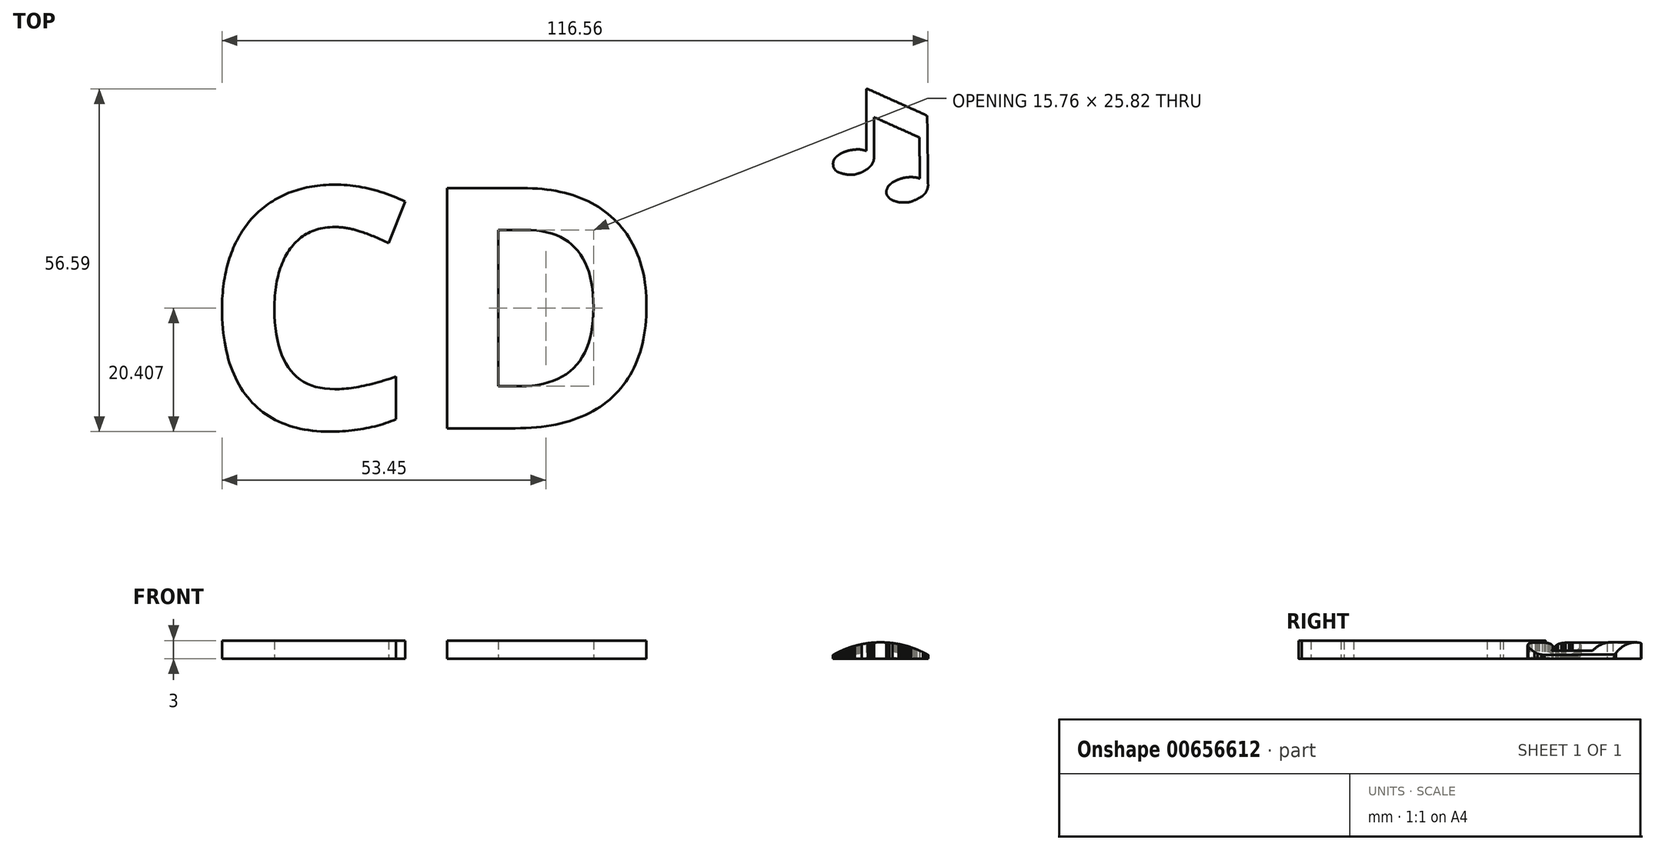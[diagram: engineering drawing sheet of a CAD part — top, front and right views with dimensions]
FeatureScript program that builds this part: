
annotation { "Feature Type Name" : "Feature", "Feature Type Description" : "" }
export const myFeature = defineFeature(function(context is Context, id is Id, definition is map)
    precondition{}
    {
        {
            var Q0;
            Q0=qCreatedBy(makeId("Top.planeOp"),FACE);
            var sketch = newSketch(context, id + "F0", { "sketchPlane" : qUnion([Q0])});
            skText(sketch, "E0", { "text": "CD", "fontName": "OpenSans-Bold.ttf"});
            const initialGuessF0  = {"E0": [-0.08042, -0.00379, 1, 0, 0.04]};
            skSetInitialGuess(sketch, initialGuessF0);
            skSolve(sketch);
        }
        {
            var Q0;
            Q0=makeQuery(id+"F0.imprint","IMPRINT",FACE,{"disambiguationData":[TD([[makeQuery(id+"F0.imprint","IMPRINT",EDGE,{"derivedFrom":sQuery(id+"F0.wireOp",EDGE,"E0.sketch_text.stroke-15")}),-1.0]])]});
            var Q1;
            Q1=makeQuery(id+"F0.imprint","IMPRINT",FACE,{"disambiguationData":[TD([[makeQuery(id+"F0.imprint","IMPRINT",EDGE,{"derivedFrom":sQuery(id+"F0.wireOp",EDGE,"E0.sketch_text.stroke-0")}),-1.0]])]});
            extrude(context, id + "F1", {"entities" : qUnion([Q0, Q1]), "depth" : 3 * mm, "offsetDistance" : 25 * mm});
        }
        {
            var Q0;
            Q0=qCreatedBy(makeId("Top.planeOp"),FACE);
            var sketch = newSketch(context, id + "F2", { "sketchPlane" : qUnion([Q0])});
            skLineSegment(sketch, "E1", {"start": v(39.37, 36.26) * mm, "end": v(39.32, 36.01) * mm});
            skLineSegment(sketch, "E2", {"start": v(39.32, 36.01) * mm, "end": v(39.27, 35.76) * mm});
            skLineSegment(sketch, "E3", {"start": v(39.27, 35.76) * mm, "end": v(38.98, 35.1) * mm});
            skLineSegment(sketch, "E4", {"start": v(38.98, 35.1) * mm, "end": v(38.39, 34.5) * mm});
            skLineSegment(sketch, "E5", {"start": v(38.39, 34.5) * mm, "end": v(38.17, 34.37) * mm});
            skLineSegment(sketch, "E6", {"start": v(38.17, 34.37) * mm, "end": v(37.95, 34.24) * mm});
            skLineSegment(sketch, "E7", {"start": v(37.95, 34.24) * mm, "end": v(37.72, 34.12) * mm});
            skLineSegment(sketch, "E8", {"start": v(37.72, 34.12) * mm, "end": v(37.5, 34.01) * mm});
            skLineSegment(sketch, "E9", {"start": v(37.5, 34.01) * mm, "end": v(37.26, 33.9) * mm});
            skLineSegment(sketch, "E10", {"start": v(37.26, 33.9) * mm, "end": v(37.03, 33.8) * mm});
            skLineSegment(sketch, "E11", {"start": v(37.03, 33.8) * mm, "end": v(36.79, 33.71) * mm});
            skLineSegment(sketch, "E12", {"start": v(36.55, 33.62) * mm, "end": v(36.42, 33.6) * mm});
            skLineSegment(sketch, "E13", {"start": v(36.42, 33.6) * mm, "end": v(36.3, 33.57) * mm});
            skLineSegment(sketch, "E14", {"start": v(36.3, 33.57) * mm, "end": v(36.17, 33.54) * mm});
            skLineSegment(sketch, "E15", {"start": v(36.17, 33.54) * mm, "end": v(36.04, 33.53) * mm});
            skLineSegment(sketch, "E16", {"start": v(36.04, 33.53) * mm, "end": v(35.91, 33.51) * mm});
            skLineSegment(sketch, "E17", {"start": v(35.91, 33.51) * mm, "end": v(35.78, 33.5) * mm});
            skLineSegment(sketch, "E18", {"start": v(35.78, 33.5) * mm, "end": v(35.65, 33.5) * mm});
            skLineSegment(sketch, "E19", {"start": v(35.65, 33.5) * mm, "end": v(35.52, 33.5) * mm});
            skLineSegment(sketch, "E20", {"start": v(35.52, 33.5) * mm, "end": v(35.26, 33.5) * mm});
            skLineSegment(sketch, "E21", {"start": v(35.26, 33.5) * mm, "end": v(35, 33.5) * mm});
            skLineSegment(sketch, "E22", {"start": v(35, 33.5) * mm, "end": v(34.74, 33.53) * mm});
            skLineSegment(sketch, "E23", {"start": v(34.74, 33.53) * mm, "end": v(34.48, 33.55) * mm});
            skLineSegment(sketch, "E24", {"start": v(34.48, 33.55) * mm, "end": v(33.53, 33.84) * mm});
            skLineSegment(sketch, "E25", {"start": v(33.53, 33.84) * mm, "end": v(33.01, 34.14) * mm});
            skLineSegment(sketch, "E26", {"start": v(33.01, 34.14) * mm, "end": v(32.57, 34.73) * mm});
            skLineSegment(sketch, "E27", {"start": v(32.57, 34.73) * mm, "end": v(32.54, 34.82) * mm});
            skLineSegment(sketch, "E28", {"start": v(32.54, 34.82) * mm, "end": v(32.52, 34.9) * mm});
            skLineSegment(sketch, "E29", {"start": v(32.52, 34.9) * mm, "end": v(32.5, 35) * mm});
            skLineSegment(sketch, "E30", {"start": v(32.5, 35) * mm, "end": v(32.49, 35.1) * mm});
            skLineSegment(sketch, "E31", {"start": v(32.49, 35.1) * mm, "end": v(32.48, 35.18) * mm});
            skLineSegment(sketch, "E32", {"start": v(32.48, 35.18) * mm, "end": v(32.48, 35.28) * mm});
            skLineSegment(sketch, "E33", {"start": v(32.48, 35.28) * mm, "end": v(32.49, 35.37) * mm});
            skLineSegment(sketch, "E34", {"start": v(32.49, 35.37) * mm, "end": v(32.5, 35.46) * mm});
            skLineSegment(sketch, "E35", {"start": v(32.5, 35.46) * mm, "end": v(32.79, 36.2) * mm});
            skLineSegment(sketch, "E36", {"start": v(32.79, 36.2) * mm, "end": v(33.45, 36.8) * mm});
            skLineSegment(sketch, "E37", {"start": v(33.45, 36.8) * mm, "end": v(33.6, 36.88) * mm});
            skLineSegment(sketch, "E38", {"start": v(33.6, 36.88) * mm, "end": v(33.76, 36.96) * mm});
            skLineSegment(sketch, "E39", {"start": v(33.76, 36.96) * mm, "end": v(33.92, 37.04) * mm});
            skLineSegment(sketch, "E40", {"start": v(33.92, 37.04) * mm, "end": v(34.08, 37.12) * mm});
            skLineSegment(sketch, "E41", {"start": v(34.08, 37.12) * mm, "end": v(34.24, 37.19) * mm});
            skLineSegment(sketch, "E42", {"start": v(34.24, 37.19) * mm, "end": v(34.4, 37.26) * mm});
            skLineSegment(sketch, "E43", {"start": v(34.4, 37.26) * mm, "end": v(34.56, 37.32) * mm});
            skLineSegment(sketch, "E44", {"start": v(34.56, 37.32) * mm, "end": v(34.73, 37.38) * mm});
            skLineSegment(sketch, "E45", {"start": v(34.73, 37.38) * mm, "end": v(34.9, 37.44) * mm});
            skLineSegment(sketch, "E46", {"start": v(34.9, 37.44) * mm, "end": v(35.07, 37.5) * mm});
            skLineSegment(sketch, "E47", {"start": v(35.07, 37.5) * mm, "end": v(35.24, 37.54) * mm});
            skLineSegment(sketch, "E48", {"start": v(35.24, 37.54) * mm, "end": v(35.4, 37.58) * mm});
            skLineSegment(sketch, "E49", {"start": v(35.4, 37.58) * mm, "end": v(35.58, 37.6) * mm});
            skLineSegment(sketch, "E50", {"start": v(35.58, 37.6) * mm, "end": v(35.75, 37.64) * mm});
            skLineSegment(sketch, "E51", {"start": v(35.75, 37.64) * mm, "end": v(35.93, 37.66) * mm});
            skLineSegment(sketch, "E52", {"start": v(35.93, 37.66) * mm, "end": v(36.1, 37.67) * mm});
            skLineSegment(sketch, "E53", {"start": v(36.1, 37.67) * mm, "end": v(36.28, 37.68) * mm});
            skLineSegment(sketch, "E54", {"start": v(36.28, 37.68) * mm, "end": v(36.45, 37.69) * mm});
            skLineSegment(sketch, "E55", {"start": v(36.45, 37.69) * mm, "end": v(36.63, 37.69) * mm});
            skLineSegment(sketch, "E56", {"start": v(36.63, 37.69) * mm, "end": v(36.8, 37.68) * mm});
            skLineSegment(sketch, "E57", {"start": v(36.8, 37.68) * mm, "end": v(36.98, 37.67) * mm});
            skLineSegment(sketch, "E58", {"start": v(36.98, 37.67) * mm, "end": v(37.16, 37.65) * mm});
            skLineSegment(sketch, "E59", {"start": v(37.16, 37.65) * mm, "end": v(37.33, 37.63) * mm});
            skLineSegment(sketch, "E60", {"start": v(37.33, 37.63) * mm, "end": v(37.5, 37.6) * mm});
            skLineSegment(sketch, "E61", {"start": v(37.5, 37.6) * mm, "end": v(38.02, 37.45) * mm});
            skLineSegment(sketch, "E62", {"start": v(38.02, 37.45) * mm, "end": v(37.94, 44.23) * mm});
            skLineSegment(sketch, "E63", {"start": v(37.94, 44.23) * mm, "end": v(32.72, 46.59) * mm});
            skLineSegment(sketch, "E64", {"start": v(32.72, 46.59) * mm, "end": v(30.46, 47.57) * mm});
            skLineSegment(sketch, "E65", {"start": v(30.46, 40.88) * mm, "end": v(30.41, 40.6) * mm});
            skLineSegment(sketch, "E66", {"start": v(30.41, 40.6) * mm, "end": v(30.36, 40.33) * mm});
            skLineSegment(sketch, "E67", {"start": v(30.36, 40.33) * mm, "end": v(30.06, 39.74) * mm});
            skLineSegment(sketch, "E68", {"start": v(30.06, 39.74) * mm, "end": v(29.99, 39.65) * mm});
            skLineSegment(sketch, "E69", {"start": v(29.99, 39.65) * mm, "end": v(29.91, 39.56) * mm});
            skLineSegment(sketch, "E70", {"start": v(29.91, 39.56) * mm, "end": v(29.83, 39.47) * mm});
            skLineSegment(sketch, "E71", {"start": v(29.83, 39.47) * mm, "end": v(29.75, 39.39) * mm});
            skLineSegment(sketch, "E72", {"start": v(29.75, 39.39) * mm, "end": v(29.67, 39.3) * mm});
            skLineSegment(sketch, "E73", {"start": v(29.67, 39.3) * mm, "end": v(29.58, 39.23) * mm});
            skLineSegment(sketch, "E74", {"start": v(29.58, 39.23) * mm, "end": v(29.5, 39.15) * mm});
            skLineSegment(sketch, "E75", {"start": v(29.5, 39.15) * mm, "end": v(29.4, 39.07) * mm});
            skLineSegment(sketch, "E76", {"start": v(29.4, 39.07) * mm, "end": v(28.44, 38.48) * mm});
            skLineSegment(sketch, "E77", {"start": v(28.44, 38.48) * mm, "end": v(27.27, 38.12) * mm});
            skLineSegment(sketch, "E78", {"start": v(27.27, 38.12) * mm, "end": v(27.08, 38.1) * mm});
            skLineSegment(sketch, "E79", {"start": v(27.08, 38.1) * mm, "end": v(26.9, 38.08) * mm});
            skLineSegment(sketch, "E80", {"start": v(26.9, 38.08) * mm, "end": v(26.72, 38.07) * mm});
            skLineSegment(sketch, "E81", {"start": v(26.72, 38.07) * mm, "end": v(26.54, 38.07) * mm});
            skLineSegment(sketch, "E82", {"start": v(26.54, 38.07) * mm, "end": v(26.36, 38.08) * mm});
            skLineSegment(sketch, "E83", {"start": v(26.36, 38.08) * mm, "end": v(26.17, 38.1) * mm});
            skLineSegment(sketch, "E84", {"start": v(26.17, 38.1) * mm, "end": v(26, 38.12) * mm});
            skLineSegment(sketch, "E85", {"start": v(26, 38.12) * mm, "end": v(25.81, 38.15) * mm});
            skLineSegment(sketch, "E86", {"start": v(25.81, 38.15) * mm, "end": v(25.63, 38.18) * mm});
            skLineSegment(sketch, "E87", {"start": v(25.63, 38.18) * mm, "end": v(25.45, 38.22) * mm});
            skLineSegment(sketch, "E88", {"start": v(25.45, 38.22) * mm, "end": v(25.27, 38.26) * mm});
            skLineSegment(sketch, "E89", {"start": v(25.27, 38.26) * mm, "end": v(25.1, 38.31) * mm});
            skLineSegment(sketch, "E90", {"start": v(25.1, 38.31) * mm, "end": v(24.92, 38.37) * mm});
            skLineSegment(sketch, "E91", {"start": v(24.92, 38.37) * mm, "end": v(24.74, 38.43) * mm});
            skLineSegment(sketch, "E92", {"start": v(24.74, 38.43) * mm, "end": v(24.57, 38.5) * mm});
            skLineSegment(sketch, "E93", {"start": v(24.57, 38.5) * mm, "end": v(24.4, 38.56) * mm});
            skLineSegment(sketch, "E94", {"start": v(24.4, 38.56) * mm, "end": v(24.03, 38.85) * mm});
            skLineSegment(sketch, "E95", {"start": v(24.03, 38.85) * mm, "end": v(23.73, 39.37) * mm});
            skLineSegment(sketch, "E96", {"start": v(23.73, 39.37) * mm, "end": v(23.71, 39.5) * mm});
            skLineSegment(sketch, "E97", {"start": v(23.71, 39.5) * mm, "end": v(23.7, 39.65) * mm});
            skLineSegment(sketch, "E98", {"start": v(23.7, 39.65) * mm, "end": v(23.69, 39.8) * mm});
            skLineSegment(sketch, "E99", {"start": v(23.69, 39.8) * mm, "end": v(23.68, 39.93) * mm});
            skLineSegment(sketch, "E100", {"start": v(23.68, 39.93) * mm, "end": v(23.7, 40.07) * mm});
            skLineSegment(sketch, "E101", {"start": v(23.7, 40.07) * mm, "end": v(23.7, 40.14) * mm});
            skLineSegment(sketch, "E102", {"start": v(23.7, 40.14) * mm, "end": v(23.71, 40.2) * mm});
            skLineSegment(sketch, "E103", {"start": v(23.71, 40.2) * mm, "end": v(23.73, 40.28) * mm});
            skLineSegment(sketch, "E104", {"start": v(23.73, 40.28) * mm, "end": v(23.75, 40.34) * mm});
            skLineSegment(sketch, "E105", {"start": v(23.75, 40.34) * mm, "end": v(23.77, 40.4) * mm});
            skLineSegment(sketch, "E106", {"start": v(23.77, 40.4) * mm, "end": v(23.8, 40.47) * mm});
            skLineSegment(sketch, "E107", {"start": v(23.8, 40.47) * mm, "end": v(23.87, 40.6) * mm});
            skLineSegment(sketch, "E108", {"start": v(23.87, 40.6) * mm, "end": v(23.93, 40.7) * mm});
            skLineSegment(sketch, "E109", {"start": v(23.93, 40.7) * mm, "end": v(23.97, 40.76) * mm});
            skLineSegment(sketch, "E110", {"start": v(23.97, 40.76) * mm, "end": v(24, 40.81) * mm});
            skLineSegment(sketch, "E111", {"start": v(24, 40.81) * mm, "end": v(24.05, 40.86) * mm});
            skLineSegment(sketch, "E112", {"start": v(24.05, 40.86) * mm, "end": v(24.1, 40.91) * mm});
            skLineSegment(sketch, "E113", {"start": v(24.1, 40.91) * mm, "end": v(24.18, 41) * mm});
            skLineSegment(sketch, "E114", {"start": v(24.18, 41) * mm, "end": v(24.27, 41.08) * mm});
            skLineSegment(sketch, "E115", {"start": v(24.27, 41.08) * mm, "end": v(24.36, 41.15) * mm});
            skLineSegment(sketch, "E116", {"start": v(24.36, 41.15) * mm, "end": v(24.45, 41.23) * mm});
            skLineSegment(sketch, "E117", {"start": v(24.45, 41.23) * mm, "end": v(24.64, 41.37) * mm});
            skLineSegment(sketch, "E118", {"start": v(24.64, 41.37) * mm, "end": v(24.84, 41.5) * mm});
            skLineSegment(sketch, "E119", {"start": v(24.84, 41.5) * mm, "end": v(24.92, 41.56) * mm});
            skLineSegment(sketch, "E120", {"start": v(24.92, 41.56) * mm, "end": v(25, 41.6) * mm});
            skLineSegment(sketch, "E121", {"start": v(25, 41.6) * mm, "end": v(25.1, 41.65) * mm});
            skLineSegment(sketch, "E122", {"start": v(25.1, 41.65) * mm, "end": v(25.18, 41.7) * mm});
            skLineSegment(sketch, "E123", {"start": v(25.18, 41.7) * mm, "end": v(25.36, 41.77) * mm});
            skLineSegment(sketch, "E124", {"start": v(25.36, 41.77) * mm, "end": v(25.55, 41.84) * mm});
            skLineSegment(sketch, "E125", {"start": v(25.55, 41.84) * mm, "end": v(25.74, 41.9) * mm});
            skLineSegment(sketch, "E126", {"start": v(25.74, 41.9) * mm, "end": v(25.93, 41.97) * mm});
            skLineSegment(sketch, "E127", {"start": v(25.93, 41.97) * mm, "end": v(26.3, 42.1) * mm});
            skLineSegment(sketch, "E128", {"start": v(26.3, 42.1) * mm, "end": v(26.55, 42.14) * mm});
            skLineSegment(sketch, "E129", {"start": v(26.55, 42.14) * mm, "end": v(26.8, 42.18) * mm});
            skLineSegment(sketch, "E130", {"start": v(26.8, 42.18) * mm, "end": v(27.05, 42.21) * mm});
            skLineSegment(sketch, "E131", {"start": v(27.05, 42.21) * mm, "end": v(27.3, 42.24) * mm});
            skLineSegment(sketch, "E132", {"start": v(27.3, 42.24) * mm, "end": v(27.55, 42.26) * mm});
            skLineSegment(sketch, "E133", {"start": v(27.55, 42.26) * mm, "end": v(27.8, 42.26) * mm});
            skLineSegment(sketch, "E134", {"start": v(27.8, 42.26) * mm, "end": v(27.92, 42.26) * mm});
            skLineSegment(sketch, "E135", {"start": v(27.92, 42.26) * mm, "end": v(28.05, 42.26) * mm});
            skLineSegment(sketch, "E136", {"start": v(28.05, 42.26) * mm, "end": v(28.17, 42.25) * mm});
            skLineSegment(sketch, "E137", {"start": v(28.17, 42.25) * mm, "end": v(28.3, 42.24) * mm});
            skLineSegment(sketch, "E138", {"start": v(28.3, 42.24) * mm, "end": v(29.18, 42.02) * mm});
            skLineSegment(sketch, "E139", {"start": v(29.18, 42.02) * mm, "end": v(29.18, 52.26) * mm});
            skLineSegment(sketch, "E140", {"start": v(29.27, 52.25) * mm, "end": v(29.37, 52.24) * mm});
            skLineSegment(sketch, "E141", {"start": v(29.37, 52.24) * mm, "end": v(29.41, 52.23) * mm});
            skLineSegment(sketch, "E142", {"start": v(29.41, 52.23) * mm, "end": v(29.46, 52.22) * mm});
            skLineSegment(sketch, "E143", {"start": v(29.46, 52.22) * mm, "end": v(29.5, 52.2) * mm});
            skLineSegment(sketch, "E144", {"start": v(29.5, 52.2) * mm, "end": v(29.55, 52.18) * mm});
            skLineSegment(sketch, "E145", {"start": v(29.55, 52.18) * mm, "end": v(34.78, 49.83) * mm});
            skLineSegment(sketch, "E146", {"start": v(34.78, 49.83) * mm, "end": v(38.75, 48.06) * mm});
            skLineSegment(sketch, "E147", {"start": v(38.75, 48.06) * mm, "end": v(39.27, 47.76) * mm});
            skLineSegment(sketch, "E148", {"start": v(39.23, 47.79) * mm, "end": v(39.37, 36.26) * mm});
            skLineSegment(sketch, "E149", {"start": v(30.46, 40.88) * mm, "end": v(30.46, 47.57) * mm});
            skCircle(sketch, "E150", {"center": v(33.02, 42.98) * mm, "radius": 10 * mm});
            skPoint(sketch, "E150.third.point", {"position": v(26.78, 35.17) * mm});
            skSolve(sketch);
        }
        {
            var Q0;
            Q0=makeQuery(id+"F2.imprint","IMPRINT",FACE,{"disambiguationData":[TD([[makeQuery(id+"F2.imprint","IMPRINT",EDGE,{"derivedFrom":sQuery(id+"F2.wireOp",EDGE,"E1")}),-1.0]])]});
            extrude(context, id + "F3", {"entities" : qUnion([Q0]), "depth" : 3 * mm, "offsetDistance" : 25 * mm});
        }
        {
            var Q0;
            Q0=qCreatedBy(makeId("Front.planeOp"),FACE);
            var sketch = newSketch(context, id + "F4", { "sketchPlane" : qUnion([Q0])});
            skCircle(sketch, "E151", {"center": v(31.54, -13.07) * mm, "radius": 15.77 * mm});
            skPoint(sketch, "E151.first.point", {"position": v(23.6, 0.55) * mm});
            skPoint(sketch, "E151.second.point", {"position": v(39.5, 0.54) * mm});
            skPoint(sketch, "E151.third.point", {"position": v(37.46, 1.54) * mm});
            skCircle(sketch, "E152.0", {"center": v(31.54, -13.07) * mm, "radius": 20.77 * mm});
            skSolve(sketch);
        }
        {
            var Q0;
            Q0 = qSketchRegion(id + "F4", true);
            extrude(context, id + "F5", {"entities" : qUnion([Q0]), "operationType" : NewBodyOperationType.REMOVE, "oppositeDirection" : true, "depth" : 57.7 * mm, "offsetDistance" : 25 * mm});
        }
    });
